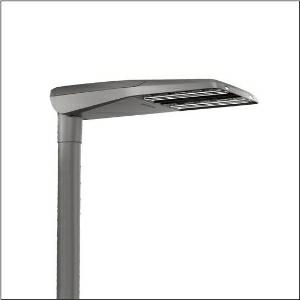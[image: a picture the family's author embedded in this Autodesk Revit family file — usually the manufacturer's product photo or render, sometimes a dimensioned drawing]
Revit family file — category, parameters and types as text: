
# Revit family: streetlight_sl_11_iq_midi___st0_5st0_5_5xc3h41e08me_4b4c
name_source: partatom
category: Lighting Fixtures
units: mm (PartAtom-declared; Revit-internal decimal feet)

## family parameters
Cut with Voids When Loaded = No
Host = Face
Light Source = No
Part Type = Normal
Room Calculation Point = No
Round Connector Dimension = Use Diameter
Shared = No

## types (1)
- --- (1 x LED, 18720 lm, 124.7 W, 4000K)
    Apparent Load = 125 VA
    CIE Flux Codes = 43 74 97 100 100
    Color Rendering = 70
    Color Temperature = 4000K
    Default Elevation = 1800 mm
    Description = Streetlight SL 11 iQ midi, mast luminaire, primary light control with 3 zone facetted reflector, of plastic, silver coated, highly specular, primary optical cover: cover, of PMMA, transparent, light distribution: ST0.5ST0.5, light emission: direct distribution, primary light characteristic: asymmetric, installation type: post-top, side-entry, LED, High Power LED, rated luminous flux: 18.720lm, luminous efficacy: 150lm/W, light colour: 740, colour temperature: 4000K, control: optimised constant luminous flux control (CLO 2.0), Desk-Remote (wireless, voltage-free reading and setting of iQ features in the workshop via application-optimized NFC function/RFID function), Light-Fading, Smart-Wire, Night-Set, Lumen-Switch, Temp-Guard, Auto-Match, with cable H07RN-F 5x 1.5mm², mains connection: 220..240V, AC, 50/60Hz, connection cable pre-assembled, cable length: 12,5m, start of lifetime: 125W, end of lifetime: 132W, reduction: 61W, luminaire housing, of diecast aluminium, powder-coated, Siteco® metallic grey (DB 702S), length: 780mm, width: 376mm, height: 118mm, spigot size: 60/76mm (post-top) and 42/60/76mm (side-entry), mast flange for spigot size: 42mm: 5XC10008XM4, 60mm: 5XC10008XM2, 76/60mm: 5XC10108XM1, equipment: Power, protection rating (complete): IP66, insulation class (complete): insulation class II (safety insulation), certification: CE, ENEC, VDE, impact resistance: IK09, permissible operating ambient temperature for outdoor applications: -25..+50°C, standard-compliant lighting for roads and squares, packaging unit: 1 piece

Light Distribution: ST0.5ST0.5
    Height = 118 mm
    Lamp = 1 x LED
    Lamp Light Flux = 18720 lm
    Lamp Power = 124.7 W
    Lamp count = 1
    Length = 780 mm
    Luminous efficacy = 150 lm/W
    Manufacturer = Siteco
    ModVariant = No
    Model = 5XC3H41E08ME
    Number of Poles = 1
    OnlyDefault = Yes
    Power Factor = 1
    Product Name = Streetlight SL 11 iQ midi | ST0.5ST0.5
    Product group = mast luminaire | pylon top
    ProductGroupID = 6100
    Protection Class = Protection class II
    Protection Degree = IP 66
    RLX_Detail_Level = 1
    RlxData = <blob elided: 75149 chars, md5=e1825580>
    Socket = socket
    Standby Power = 0 W
    System Light Flux = 18720 lm
    System Power = 125 W
    Type Comments = factory setting: luminous flux: 100 % | dim-lin: 254 | 557 mA
    Type Image = l_1005960.jpg
    URL = http://relux.com
    VarID = @adj_086551
    Voltage = 0 V
    Weight = 0.00 kg
    Width = 376 mm

## geometry (parser evidence)
native form markers: Blend x4, Sweep x12
no freeform markers — native parametric forms only
